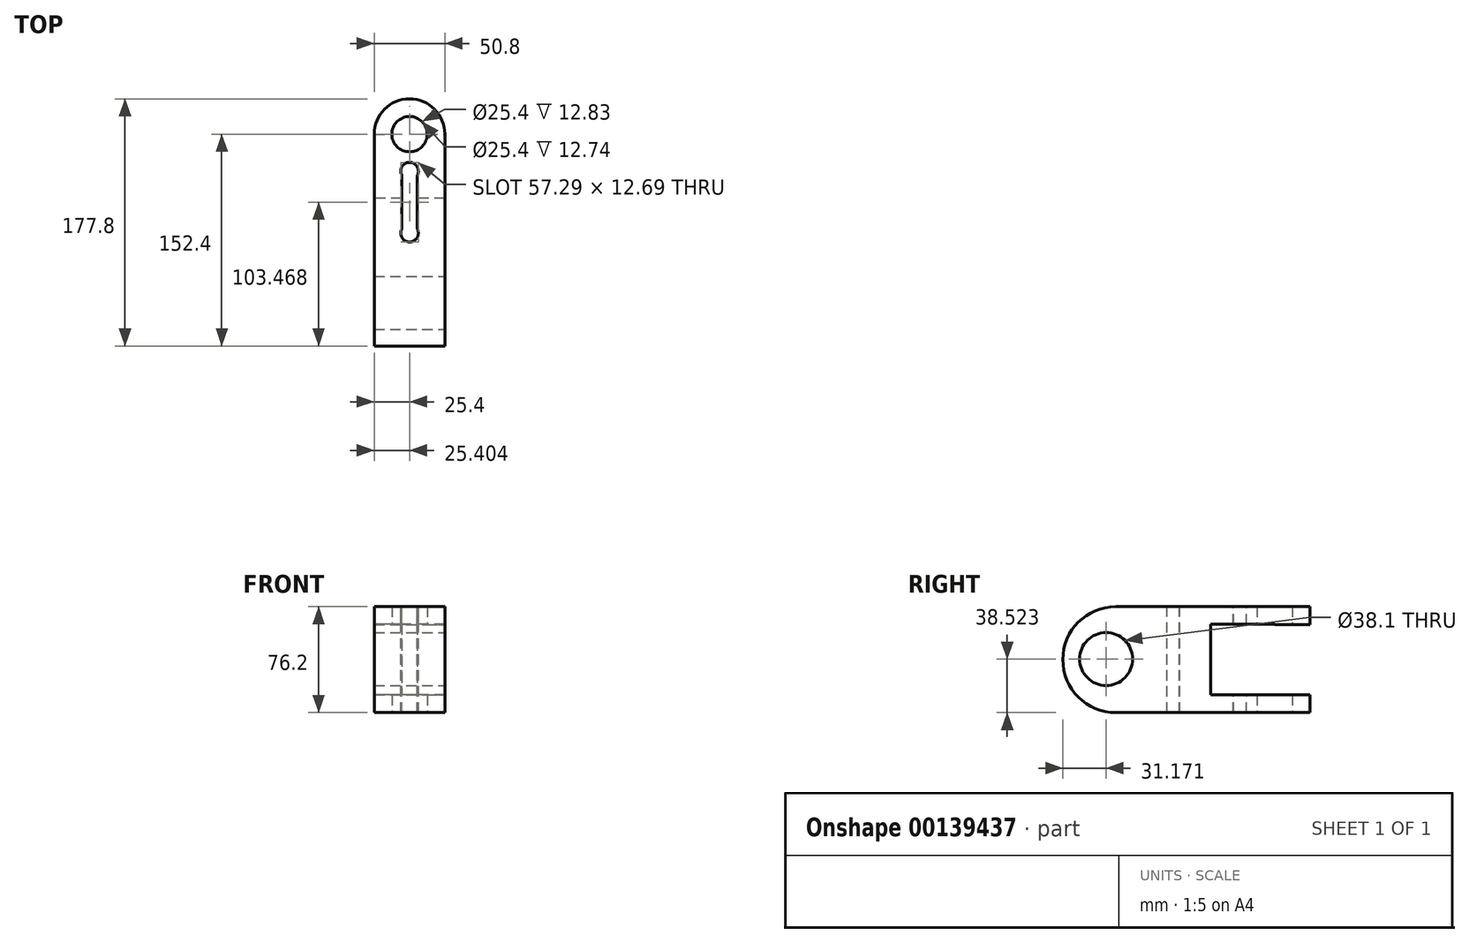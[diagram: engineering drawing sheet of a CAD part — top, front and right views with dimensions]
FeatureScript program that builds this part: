
annotation { "Feature Type Name" : "Feature", "Feature Type Description" : "" }
export const myFeature = defineFeature(function(context is Context, id is Id, definition is map)
    precondition{}
    {
        {
            var Q0;
            Q0=qCreatedBy(makeId("Top.planeOp"),FACE);
            var sketch = newSketch(context, id + "F0", { "sketchPlane" : qUnion([Q0])});
            skCircle(sketch, "E0", {"center": v(0, 0) * mm, "radius": 12.7 * mm});
            skArc(sketch, "E1", {"start": v(25.4, 0) * mm, "mid": v(0, 25.4) * mm, "end": v(-25.4, 0) * mm});
            skLineSegment(sketch, "E2", {"start": v(-25.4, 0) * mm, "end": v(-25.4, -152.4) * mm});
            skLineSegment(sketch, "E3", {"start": v(25.4, 0) * mm, "end": v(25.4, -152.4) * mm});
            skLineSegment(sketch, "E4", {"start": v(-25.4, -152.4) * mm, "end": v(25.4, -152.4) * mm});
            skSolve(sketch);
        }
        {
            var Q0;
            Q0 = qSketchRegion(id + "F0", true);
            extrude(context, id + "F1", {"entities" : qUnion([Q0]), "depth" : 76.2 * mm});
        }
        {
            var Q0;
            Q0=makeQuery(id+"F1.opExtrude","CAP_EDGE",EDGE,{"disambiguationData":[OSD([sQuery(id+"F0.wireOp",EDGE,"E4")])],"isStart":false});
            var Q1;
            Q1=makeQuery(id+"F1.opExtrude","CAP_EDGE",EDGE,{"disambiguationData":[OSD([sQuery(id+"F0.wireOp",EDGE,"E4")])],"isStart":true});
            fillet(context, id + "F2", {"entities" : qUnion([Q0, Q1]), "radius" : 38.1 * mm, "tangentPropagation" : true, "allowEdgeOverflow" : false});
        }
        {
            var Q0;
            Q0=makeQuery(id+"F1.opExtrude","SWEPT_FACE",FACE,{"disambiguationData":[OSD([sQuery(id+"F0.wireOp",EDGE,"E3")])]});
            var sketch = newSketch(context, id + "F3", { "sketchPlane" : qUnion([Q0])});
            skCircle(sketch, "E5", {"center": v(-121.23, 38.52) * mm, "radius": 19.05 * mm});
            skSolve(sketch);
        }
        {
            var Q0;
            Q0=makeQuery(id+"F3.imprint","IMPRINT",FACE,{"disambiguationData":[TD([[makeQuery(id+"F3.imprint","IMPRINT",EDGE,{"derivedFrom":sQuery(id+"F3.wireOp",EDGE,"E5")}),1.0]])]});
            extrude(context, id + "F4", {"entities" : qUnion([Q0]), "operationType" : NewBodyOperationType.REMOVE, "endBound" : BoundingType.THROUGH_ALL, "oppositeDirection" : true, "depth" : 25.4 * mm});
        }
        {
            var Q0;
            Q0=makeQuery(id+"F1.opExtrude","CAP_FACE",FACE,{"disambiguationData":[OSD([sQuery(id+"F0.wireOp",EDGE,"E0"),sQuery(id+"F0.wireOp",EDGE,"E1"),sQuery(id+"F0.wireOp",EDGE,"E2"),sQuery(id+"F0.wireOp",EDGE,"E3"),sQuery(id+"F0.wireOp",EDGE,"E4")])],"isStart":false});
            var sketch = newSketch(context, id + "F5", { "sketchPlane" : qUnion([Q0])});
            skArc(sketch, "E6", {"start": v(-5.69, -68.4) * mm, "mid": v(0.07, -77.58) * mm, "end": v(5.62, -68.28) * mm});
            skArc(sketch, "E7", {"start": v(5.57, -29.68) * mm, "mid": v(0.18, -20.29) * mm, "end": v(-5.74, -29.35) * mm});
            skLineSegment(sketch, "E8", {"start": v(-5.74, -29.35) * mm, "end": v(-5.69, -68.4) * mm});
            skLineSegment(sketch, "E9", {"start": v(5.57, -29.68) * mm, "end": v(5.62, -68.28) * mm});
            skSolve(sketch);
        }
        {
            var Q0;
            Q0 = qSketchRegion(id + "F5", true);
            extrude(context, id + "F6", {"entities" : qUnion([Q0]), "operationType" : NewBodyOperationType.REMOVE, "endBound" : BoundingType.THROUGH_ALL, "oppositeDirection" : true, "depth" : 25.4 * mm});
        }
        {
            var Q0;
            Q0=makeQuery(id+"F1.opExtrude","SWEPT_FACE",FACE,{"disambiguationData":[OSD([sQuery(id+"F0.wireOp",EDGE,"E2")])]});
            var sketch = newSketch(context, id + "F7", { "sketchPlane" : qUnion([Q0])});
            skLineSegment(sketch, "E10", {"start": v(0, 12.7) * mm, "end": v(13, 12.7) * mm});
            skLineSegment(sketch, "E11", {"start": v(13, 63.5) * mm, "end": v(0, 63.5) * mm});
            skLineSegment(sketch, "E12", {"start": v(13, 63.5) * mm, "end": v(46.05, 63.5) * mm});
            skLineSegment(sketch, "E13", {"start": v(46.05, 63.5) * mm, "end": v(46.05, 12.63) * mm});
            skLineSegment(sketch, "E14", {"start": v(46.05, 12.63) * mm, "end": v(13, 12.7) * mm});
            skSolve(sketch);
        }
        {
            var Q0;
            {var subQ0=sQuery(id+"F7.wireOp",EDGE,"E10");Q0=makeQuery(id+"F7.imprint","IMPRINT",FACE,{"disambiguationData":[TD([[makeQuery(id+"F7.imprint","IMPRINT",EDGE,{"derivedFrom":subQ0}),1.0]])]});}
            extrude(context, id + "F8", {"entities" : qUnion([Q0]), "operationType" : NewBodyOperationType.REMOVE, "endBound" : BoundingType.THROUGH_ALL, "oppositeDirection" : true, "depth" : 25.4 * mm});
        }
        {
            var Q0;
            Q0=qCreatedBy(makeId("Right.planeOp"),FACE);
            cPlane(context, id + "F9", {"entities" : qUnion([Q0]), "cplaneType" : CPlaneType.OFFSET, "offset" : 25.4 * mm, "width" : 152.4 * mm, "height" : 152.4 * mm});
        }
        {
            var Q0;
            Q0=qCreatedBy(id+"F9.planeOp",FACE);
            var sketch = newSketch(context, id + "F10", { "sketchPlane" : qUnion([Q0])});
            skLineSegment(sketch, "E15", {"start": v(0, 63.37) * mm, "end": v(25.43, 63.37) * mm});
            skLineSegment(sketch, "E16", {"start": v(0, 12.74) * mm, "end": v(25.44, 12.74) * mm});
            skLineSegment(sketch, "E17", {"start": v(0, 63.37) * mm, "end": v(0, 12.74) * mm});
            skLineSegment(sketch, "E18", {"start": v(25.43, 63.37) * mm, "end": v(25.44, 12.74) * mm});
            skSolve(sketch);
        }
        {
            var Q0;
            Q0 = qSketchRegion(id + "F10", true);
            extrude(context, id + "F11", {"entities" : qUnion([Q0]), "operationType" : NewBodyOperationType.REMOVE, "endBound" : BoundingType.THROUGH_ALL, "oppositeDirection" : true, "depth" : 25.4 * mm});
        }
    });
